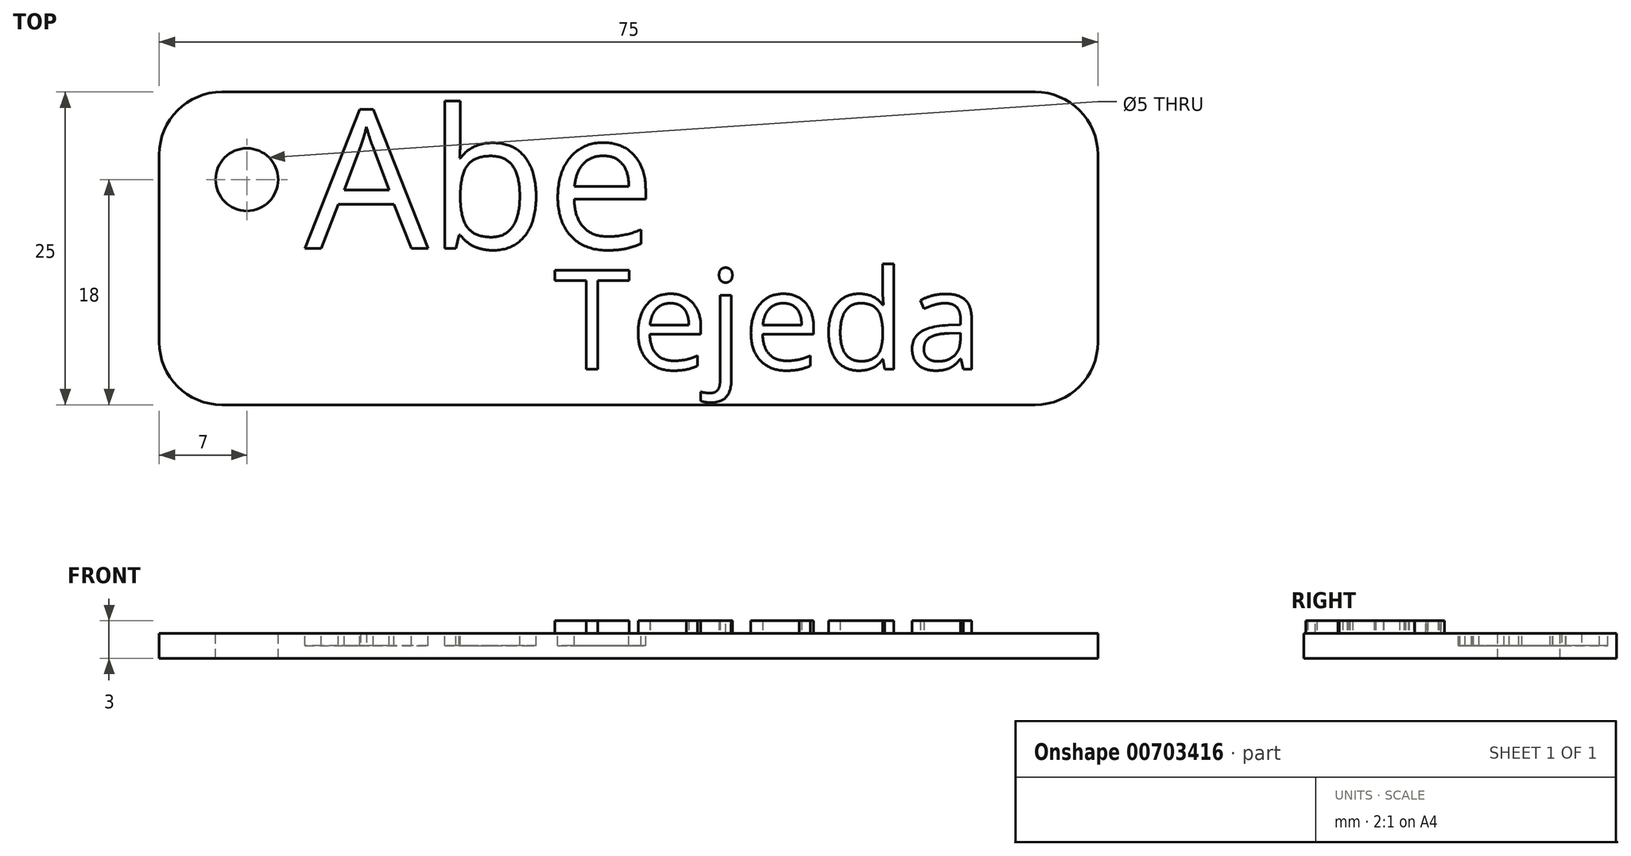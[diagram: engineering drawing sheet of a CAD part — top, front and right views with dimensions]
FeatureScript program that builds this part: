
annotation { "Feature Type Name" : "Feature", "Feature Type Description" : "" }
export const myFeature = defineFeature(function(context is Context, id is Id, definition is map)
    precondition{}
    {
        {
            var Q0;
            Q0=qCreatedBy(makeId("Top.planeOp"),FACE);
            var sketch = newSketch(context, id + "F0", { "sketchPlane" : qUnion([Q0])});
            skLineSegment(sketch, "E0.bottom", {"start": v(-32.5, 12.5) * mm, "end": v(32.5, 12.5) * mm});
            skLineSegment(sketch, "E0.top", {"start": v(-32.5, -12.5) * mm, "end": v(32.5, -12.5) * mm});
            skLineSegment(sketch, "E0.left", {"start": v(-37.5, 7.5) * mm, "end": v(-37.5, -7.5) * mm});
            skLineSegment(sketch, "E0.right", {"start": v(37.5, 7.5) * mm, "end": v(37.5, -7.5) * mm});
            skPoint(sketch, "E0.middle", {"position": v(0, 0) * mm});
            skPoint(sketch, "E1.visualSharp", {"position": v(-37.5, 12.5) * mm});
            skArc(sketch, "E1.filletArc", {"start": v(-32.5, 12.5) * mm, "mid": v(-36.04, 11.04) * mm, "end": v(-37.5, 7.5) * mm});
            skPoint(sketch, "E2.visualSharp", {"position": v(37.5, 12.5) * mm});
            skArc(sketch, "E2.filletArc", {"start": v(37.5, 7.5) * mm, "mid": v(36.04, 11.04) * mm, "end": v(32.5, 12.5) * mm});
            skPoint(sketch, "E3.visualSharp", {"position": v(37.5, -12.5) * mm});
            skArc(sketch, "E3.filletArc", {"start": v(32.5, -12.5) * mm, "mid": v(36.04, -11.04) * mm, "end": v(37.5, -7.5) * mm});
            skPoint(sketch, "E4.visualSharp", {"position": v(-37.5, -12.5) * mm});
            skArc(sketch, "E4.filletArc", {"start": v(-37.5, -7.5) * mm, "mid": v(-36.04, -11.04) * mm, "end": v(-32.5, -12.5) * mm});
            skSolve(sketch);
        }
        {
            var Q0;
            Q0=makeQuery(id+"F0.imprint","IMPRINT",FACE,{"disambiguationData":[TD([[makeQuery(id+"F0.imprint","IMPRINT",EDGE,{"derivedFrom":sQuery(id+"F0.wireOp",EDGE,"E0.bottom")}),-1.0]])]});
            extrude(context, id + "F1", {"entities" : qUnion([Q0]), "depth" : 2 * mm, "offsetDistance" : 25 * mm});
        }
        {
            var Q0;
            Q0=makeQuery(id+"F1.opExtrude","CAP_FACE",FACE,{"disambiguationData":[OSD([sQuery(id+"F0.wireOp",EDGE,"E0.bottom"),sQuery(id+"F0.wireOp",EDGE,"E0.top"),sQuery(id+"F0.wireOp",EDGE,"E0.left"),sQuery(id+"F0.wireOp",EDGE,"E0.right"),sQuery(id+"F0.wireOp",EDGE,"E1.filletArc"),sQuery(id+"F0.wireOp",EDGE,"E2.filletArc"),sQuery(id+"F0.wireOp",EDGE,"E3.filletArc"),sQuery(id+"F0.wireOp",EDGE,"E4.filletArc")])],"isStart":false});
            var sketch = newSketch(context, id + "F2", { "sketchPlane" : qUnion([Q0])});
            skPoint(sketch, "E5", {"position": v(-30.5, 5.5) * mm});
            skSolve(sketch);
        }
        {
            var Q0;
            Q0=sQuery(id+"F2.wireOp",VERTEX,"E5");
            var Q1;
            Q1=makeQuery(id+"F1.opExtrude","SWEPT_BODY",BODY,{"disambiguationData":[OSD([sQuery(id+"F0.wireOp",EDGE,"E0.bottom"),sQuery(id+"F0.wireOp",EDGE,"E0.top"),sQuery(id+"F0.wireOp",EDGE,"E0.left"),sQuery(id+"F0.wireOp",EDGE,"E0.right"),sQuery(id+"F0.wireOp",EDGE,"E1.filletArc"),sQuery(id+"F0.wireOp",EDGE,"E2.filletArc"),sQuery(id+"F0.wireOp",EDGE,"E3.filletArc"),sQuery(id+"F0.wireOp",EDGE,"E4.filletArc")])]});
            hole(context, id + "F3", {"style" : HoleStyle.SIMPLE, "endStyle" : HoleEndStyle.THROUGH, "holeDiameter" : 5 * mm, "majorDiameter" : 5 * mm, "isTappedThrough" : true, "tappedDepth" : 12 * mm, "tapClearance" : 3, "locations" : qUnion([Q0]), "scope" : qUnion([Q1])});
        }
        {
            var Q0;
            Q0=makeQuery(id+"F1.opExtrude","CAP_FACE",FACE,{"disambiguationData":[OSD([sQuery(id+"F0.wireOp",EDGE,"E0.bottom"),sQuery(id+"F0.wireOp",EDGE,"E0.top"),sQuery(id+"F0.wireOp",EDGE,"E0.left"),sQuery(id+"F0.wireOp",EDGE,"E0.right"),sQuery(id+"F0.wireOp",EDGE,"E1.filletArc"),sQuery(id+"F0.wireOp",EDGE,"E2.filletArc"),sQuery(id+"F0.wireOp",EDGE,"E3.filletArc"),sQuery(id+"F0.wireOp",EDGE,"E4.filletArc")])],"isStart":false});
            var sketch = newSketch(context, id + "F4", { "sketchPlane" : qUnion([Q0])});
            skText(sketch, "E6", { "text": "Abe", "fontName": "OpenSans-Regular.ttf"});
            const initialGuessF4  = {"E6": [-0.02585, 0, 1, 0, 0.01117]};
            skSetInitialGuess(sketch, initialGuessF4);
            skSolve(sketch);
        }
        {
            var Q0;
            Q0 = qSketchRegion(id + "F4", true);
            extrude(context, id + "F5", {"entities" : qUnion([Q0]), "operationType" : NewBodyOperationType.REMOVE, "oppositeDirection" : true, "depth" : 1 * mm, "offsetDistance" : 25 * mm});
        }
        {
            var Q0;
            {var subQ0=sQuery(id+"F0.wireOp",EDGE,"E0.left");var subQ1=sQuery(id+"F0.wireOp",EDGE,"E0.top");var subQ2=sQuery(id+"F0.wireOp",EDGE,"E0.right");var subQ3=sQuery(id+"F0.wireOp",EDGE,"E0.bottom");var subQ4=sQuery(id+"F0.wireOp",EDGE,"E1.filletArc");var subQ5=sQuery(id+"F0.wireOp",EDGE,"E2.filletArc");var subQ6=sQuery(id+"F0.wireOp",EDGE,"E4.filletArc");var subQ7=sQuery(id+"F0.wireOp",EDGE,"E3.filletArc");Q0=makeQuery(id+"F5.boolean.opBoolean","SPLIT",FACE,{"disambiguationData":[TD([makeQuery(id+"F1.opExtrude","SWEPT_FACE",FACE,{"disambiguationData":[OSD([subQ3])]})])],"derivedFrom":makeQuery(id+"F1.opExtrude","CAP_FACE",FACE,{"disambiguationData":[OSD([subQ3,subQ1,subQ0,subQ2,subQ4,subQ5,subQ7,subQ6])],"isStart":false})});}
            var sketch = newSketch(context, id + "F6", { "sketchPlane" : qUnion([Q0])});
            skText(sketch, "E7", { "text": "Tejeda", "fontName": "OpenSans-Regular.ttf"});
            const initialGuessF6  = {"E7": [-0.00598, -0.00966, 1, 0, 0.00797]};
            skSetInitialGuess(sketch, initialGuessF6);
            skSolve(sketch);
        }
        {
            var Q0;
            Q0 = qSketchRegion(id + "F6", true);
            extrude(context, id + "F7", {"entities" : qUnion([Q0]), "operationType" : NewBodyOperationType.ADD, "depth" : 1 * mm, "offsetDistance" : 25 * mm});
        }
    });
